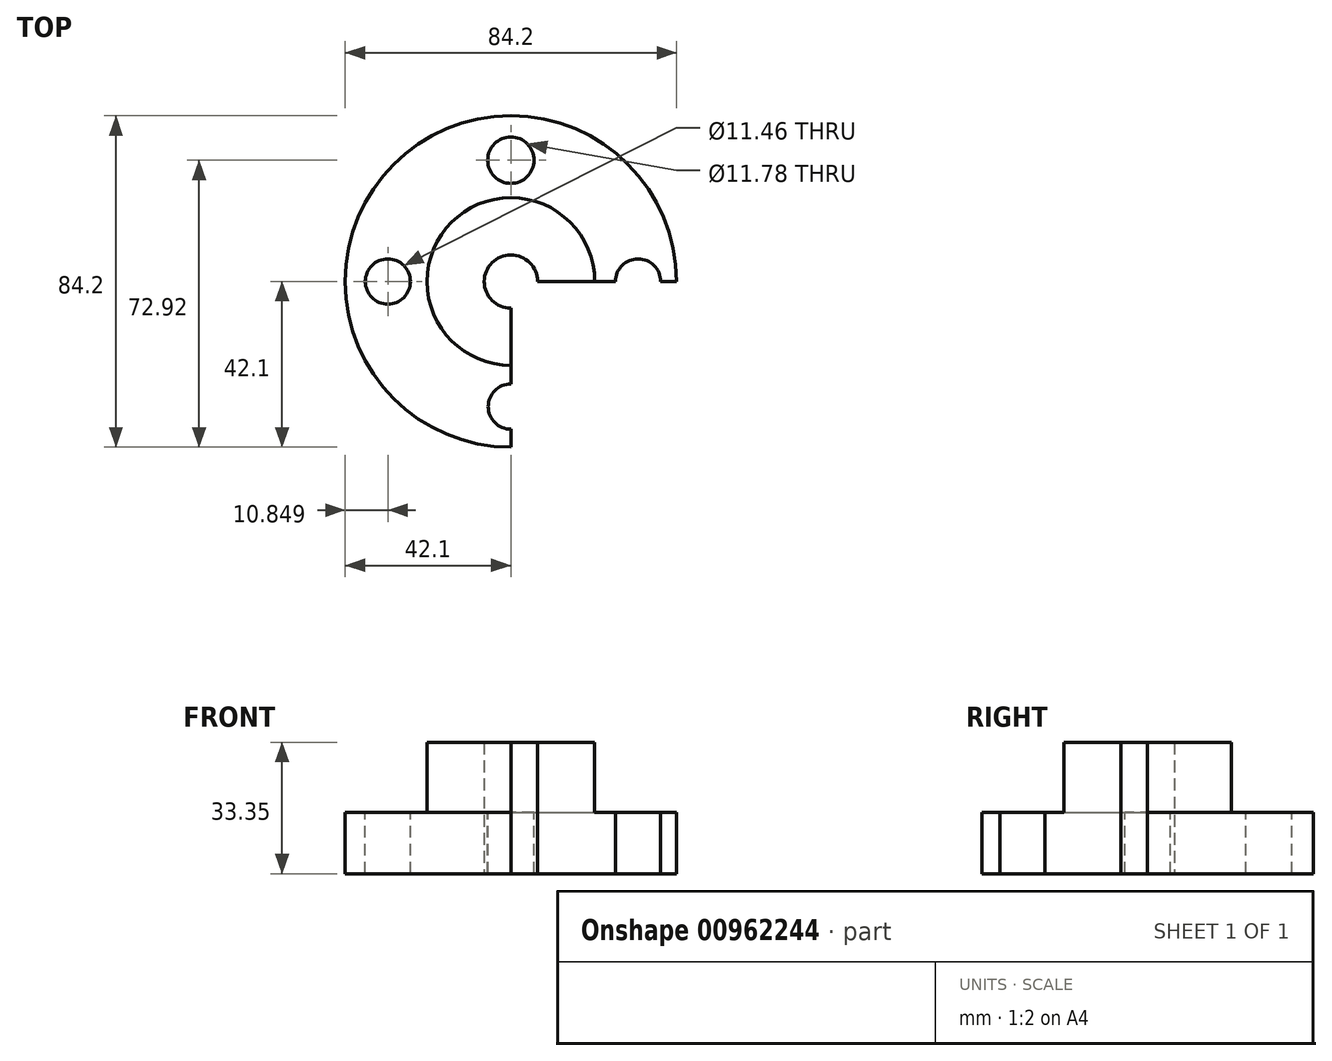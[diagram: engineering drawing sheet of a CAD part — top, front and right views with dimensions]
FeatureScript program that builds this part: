
annotation { "Feature Type Name" : "Feature", "Feature Type Description" : "" }
export const myFeature = defineFeature(function(context is Context, id is Id, definition is map)
    precondition{}
    {
        {
            var Q0;
            Q0=qCreatedBy(makeId("Front.planeOp"),FACE);
            var sketch = newSketch(context, id + "F0", { "sketchPlane" : qUnion([Q0])});
            skLineSegment(sketch, "E0.bottom", {"start": v(6.77, 0) * mm, "end": v(42.1, 0) * mm});
            skLineSegment(sketch, "E0.top", {"start": v(21.3, 15.52) * mm, "end": v(42.1, 15.52) * mm});
            skLineSegment(sketch, "E0.left", {"start": v(6.77, 0) * mm, "end": v(6.77, 15.52) * mm});
            skLineSegment(sketch, "E0.right", {"start": v(42.1, 0) * mm, "end": v(42.1, 15.52) * mm});
            skLineSegment(sketch, "E1.top", {"start": v(6.77, 33.35) * mm, "end": v(21.3, 33.35) * mm});
            skLineSegment(sketch, "E1.left", {"start": v(6.77, 15.52) * mm, "end": v(6.77, 33.35) * mm});
            skLineSegment(sketch, "E1.right", {"start": v(21.3, 15.52) * mm, "end": v(21.3, 33.35) * mm});
            skLineSegment(sketch, "E2", {"start": v(0, 0) * mm, "end": v(0, 28.54) * mm});
            skSolve(sketch);
        }
        {
            var Q0;
            Q0=makeQuery(id+"F0.imprint","IMPRINT",FACE,{"disambiguationData":[TD([[makeQuery(id+"F0.imprint","IMPRINT",EDGE,{"derivedFrom":sQuery(id+"F0.wireOp",EDGE,"E0.bottom")}),1.0]])]});
            var Q1;
            Q1=sQuery(id+"F0.wireOp",EDGE,"E2");
            revolve(context, id + "F1", {"surfaceOperationType" : NewSurfaceOperationType.NEW, "entities" : qUnion([Q0]), "axis" : qUnion([Q1]), "revolveType" : RevolveType.ONE_DIRECTION, "angle" : 270 * degree});
        }
        {
            var Q0;
            Q0=makeQuery(id+"F1.opRevolve","SWEPT_FACE",FACE,{"disambiguationData":[OSD([sQuery(id+"F0.wireOp",EDGE,"E0.top")])]});
            var sketch = newSketch(context, id + "F2", { "sketchPlane" : qUnion([Q0])});
            skPoint(sketch, "E3.center.orphan", {"position": v(0, 30.82) * mm});
            skPoint(sketch, "E4.center.orphan", {"position": v(32.31, 0) * mm});
            skPoint(sketch, "E5.center.orphan", {"position": v(-31.25, 0) * mm});
            skCircle(sketch, "E6", {"center": v(0, 30.82) * mm, "radius": 5.9 * mm});
            skCircle(sketch, "E7", {"center": v(-31.25, 0) * mm, "radius": 5.73 * mm});
            skCircle(sketch, "E8", {"center": v(0, -31.78) * mm, "radius": 5.75 * mm});
            skCircle(sketch, "E9", {"center": v(32.31, 0) * mm, "radius": 5.73 * mm});
            skSolve(sketch);
        }
        {
            var Q0;
            Q0 = qSketchRegion(id + "F2", true);
            extrude(context, id + "F3", {"entities" : qUnion([Q0]), "operationType" : NewBodyOperationType.REMOVE, "oppositeDirection" : true, "depth" : 25 * mm, "offsetDistance" : 25 * mm});
        }
    });
